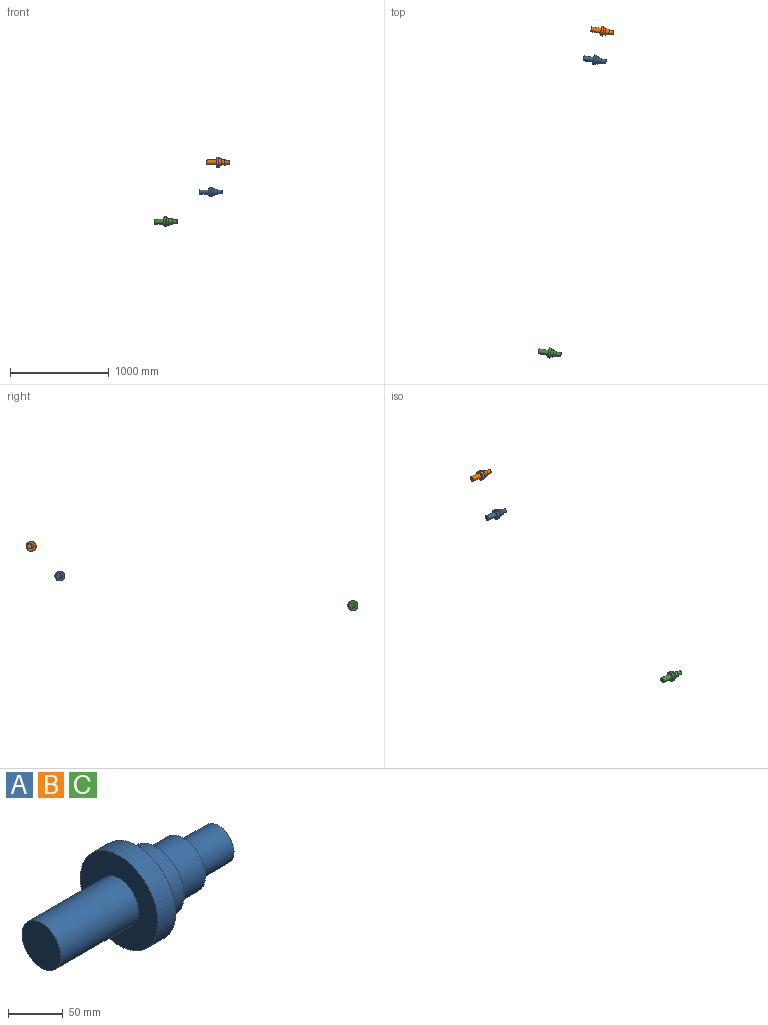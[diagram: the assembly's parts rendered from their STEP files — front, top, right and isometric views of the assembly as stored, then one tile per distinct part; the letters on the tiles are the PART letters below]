
ASSEMBLY  parts=3 mates=2
PART A: 11 faces, bbox 227.7x100x100 mm
  f0: cylinder r=28.3mm len=56.59mm, axis (-1,0,0), area 6222.5mm2, adj f7,f9
  f1: cylinder r=50mm len=100mm, axis (-1,0,0), area 7126.6mm2, adj f4,f6
  f2: cylinder r=25mm len=100mm, axis (-1,0,0), area 15708mm2, adj f3,f4
  f3: plane 50x50mm, normal (-1,0,0), area 1963.5mm2, adj f2
  f4: plane 100x100mm, normal (-1,0,0), area 5890.5mm2, adj f1,f2
  f5: cylinder r=36mm len=72mm, axis (1,0,0), area 5654.9mm2, adj f6,f7
  f6: plane 100x100mm, normal (1,0,0), area 3782.5mm2, adj f1,f5
  f7: plane 72x72mm, normal (1,0,0), area 1556.2mm2, adj f0,f5
  f8: cylinder r=20mm len=45mm, axis (1,0,0), area 5654.9mm2, adj f9,f10
  f9: plane 56.59x56.59mm, normal (1,0,0), area 1258.6mm2, adj f0,f8
  f10: plane 40x40mm, normal (1,0,0), area 1256.6mm2, adj f8
PART B: same geometry as A
PART C: same geometry as A
PLACE A rot(axis=(0,0,-1),8.7deg) t=(-331.74,-280.24,52.41)mm
PLACE B rot(axis=(-0.99,0.08,-0.13),60.6deg) t=(-256.52,11.72,352.41)mm
PLACE C rot(axis=(-0.99,0.08,-0.08),90.3deg) t=(-787.48,-3245.42,-247.59)mm
MATE planar B.f8 <-> A.f5  axis (0.99,-0.15,0) through (-31.47,-22.87,352.41)mm
MATE parallel C.f2 <-> A.f2  axis (-0.99,0.15,0) through (-787.48,-3245.42,-247.59)mm
